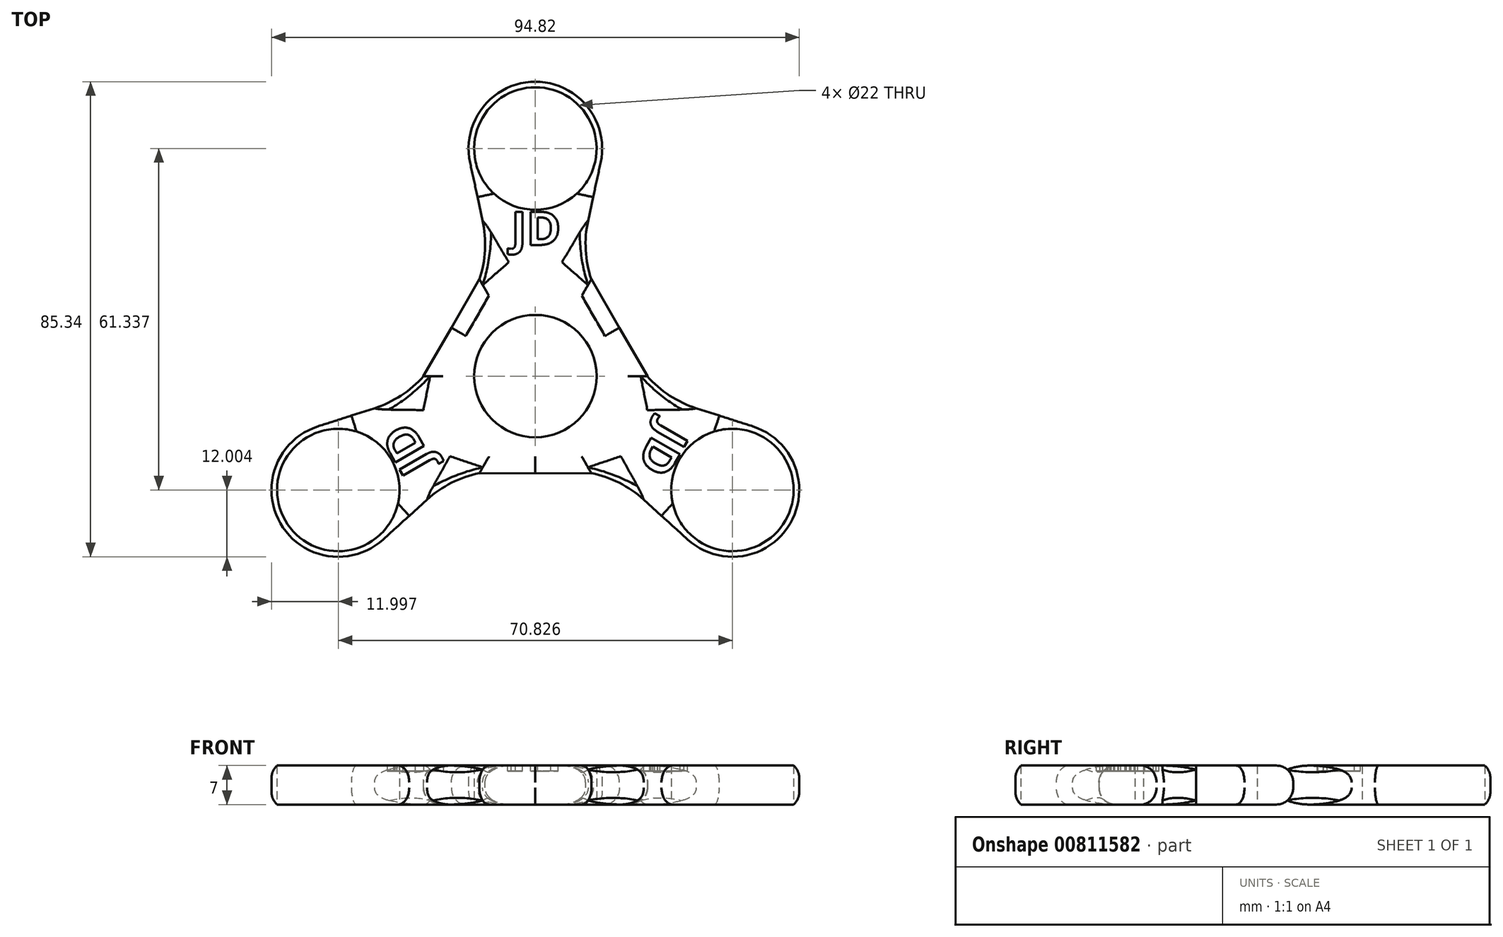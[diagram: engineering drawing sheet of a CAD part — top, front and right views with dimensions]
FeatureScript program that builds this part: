
annotation { "Feature Type Name" : "Feature", "Feature Type Description" : "" }
export const myFeature = defineFeature(function(context is Context, id is Id, definition is map)
    precondition{}
    {
        {
            var Q0;
            Q0=qCreatedBy(makeId("Top.planeOp"),FACE);
            var sketch = newSketch(context, id + "F0", { "sketchPlane" : qUnion([Q0])});
            skCircle(sketch, "E0", {"center": v(0, 0) * mm, "radius": 11 * mm});
            skCircle(sketch, "E1", {"center": v(0, 40.9) * mm, "radius": 11 * mm});
            skLineSegment(sketch, "E2", {"start": v(11, 0) * mm, "end": v(20.17, 0) * mm});
            skLineSegment(sketch, "E3", {"start": v(20.17, 0) * mm, "end": v(7.96, 20.98) * mm});
            skCircle(sketch, "E4", {"center": v(0, 40.9) * mm, "radius": 12 * mm});
            skLineSegment(sketch, "E5", {"start": v(7.96, 20.98) * mm, "end": v(11.73, 38.35) * mm});
            skLineSegment(sketch, "E6.MirrorCS", {"start": v(-11, 0) * mm, "end": v(-20.17, 0) * mm});
            skLineSegment(sketch, "E7.MirrorCS", {"start": v(-20.17, 0) * mm, "end": v(-7.96, 20.98) * mm});
            skLineSegment(sketch, "E8.MirrorCS", {"start": v(-7.96, 20.98) * mm, "end": v(-11.73, 38.35) * mm});
            skSolve(sketch);
        }
        {
            assignVariable(context, id + "F1", {"name" : "Ex", "anyValue" : 7});
        }
        {
            var Q0;
            {var subQ2=sQuery(id+"F0.wireOp",EDGE,"E2");Q0=makeQuery(id+"F0.imprint","IMPRINT",FACE,{"disambiguationData":[TD([[makeQuery(id+"F0.imprint","IMPRINT",EDGE,{"derivedFrom":subQ2}),1.0]])]});}
            var Q1;
            Q1=makeQuery(id+"F0.imprint","IMPRINT",FACE,{"disambiguationData":[TD([[makeQuery(id+"F0.imprint","IMPRINT",EDGE,{"derivedFrom":sQuery(id+"F0.wireOp",EDGE,"E1")}),-1.0]])]});
            extrude(context, id + "F2", {"entities" : qUnion([Q0, Q1]), "depth" : (getVariable(context, 'Ex')) * mm, "offsetDistance" : 25 * mm});
        }
        {
            var Q0;
            Q0=makeQuery(id+"F2.opExtrude","CAP_EDGE",EDGE,{"disambiguationData":[OSD([sQuery(id+"F0.wireOp",EDGE,"E7.MirrorCS")])],"isStart":false});
            var Q1;
            Q1=makeQuery(id+"F2.opExtrude","CAP_EDGE",EDGE,{"disambiguationData":[OSD([sQuery(id+"F0.wireOp",EDGE,"E8.MirrorCS")])],"isStart":false});
            var Q2;
            Q2=makeQuery(id+"F2.opExtrude","CAP_EDGE",EDGE,{"disambiguationData":[OSD([sQuery(id+"F0.wireOp",EDGE,"E3")])],"isStart":false});
            var Q3;
            Q3=makeQuery(id+"F2.opExtrude","CAP_EDGE",EDGE,{"disambiguationData":[OSD([sQuery(id+"F0.wireOp",EDGE,"E8.MirrorCS")])],"isStart":true});
            var Q4;
            Q4=makeQuery(id+"F2.opExtrude","CAP_EDGE",EDGE,{"disambiguationData":[OSD([sQuery(id+"F0.wireOp",EDGE,"E7.MirrorCS")])],"isStart":true});
            var Q5;
            Q5=makeQuery(id+"F2.opExtrude","CAP_EDGE",EDGE,{"disambiguationData":[OSD([sQuery(id+"F0.wireOp",EDGE,"E3")])],"isStart":true});
            fillet(context, id + "F3", {"entities" : qUnion([Q0, Q1, Q2, Q3, Q4, Q5]), "radius" : 3 * mm, "tangentPropagation" : true, "allowEdgeOverflow" : false});
        }
        {
            var Q0;
            Q0=makeQuery(id+"F2.opExtrude","CAP_FACE",FACE,{"disambiguationData":[OSD([sQuery(id+"F0.wireOp",EDGE,"E2"),sQuery(id+"F0.wireOp",EDGE,"E3"),sQuery(id+"F0.wireOp",EDGE,"E5"),sQuery(id+"F0.wireOp",EDGE,"E1"),sQuery(id+"F0.wireOp",EDGE,"E6.MirrorCS"),sQuery(id+"F0.wireOp",EDGE,"E4"),sQuery(id+"F0.wireOp",EDGE,"E0"),sQuery(id+"F0.wireOp",EDGE,"E7.MirrorCS"),sQuery(id+"F0.wireOp",EDGE,"E8.MirrorCS")])],"isStart":false});
            var sketch = newSketch(context, id + "F4", { "sketchPlane" : qUnion([Q0])});
            skText(sketch, "E9", { "text": "JD", "fontName": "NotoSans-Bold.ttf"});
            const initialGuessF4  = {"E9": [-0.00434, 0.02357, 1, 0, 0.006]};
            skSetInitialGuess(sketch, initialGuessF4);
            skSolve(sketch);
        }
        {
            var Q0;
            Q0=makeQuery(id+"F4.imprint","IMPRINT",FACE,{"disambiguationData":[TD([[makeQuery(id+"F4.imprint","IMPRINT",EDGE,{"derivedFrom":sQuery(id+"F4.wireOp",EDGE,"E9.sketch_text.stroke-0")}),-1.0]])]});
            var Q1;
            Q1=makeQuery(id+"F4.imprint","IMPRINT",FACE,{"disambiguationData":[TD([[makeQuery(id+"F4.imprint","IMPRINT",EDGE,{"derivedFrom":sQuery(id+"F4.wireOp",EDGE,"E9.sketch_text.stroke-10")}),-1.0]])]});
            extrude(context, id + "F5", {"entities" : qUnion([Q0, Q1]), "operationType" : NewBodyOperationType.REMOVE, "oppositeDirection" : true, "depth" : 1 * mm, "offsetDistance" : 25 * mm});
        }
        {
            var Q0;
            Q0=makeQuery(id+"F2.opExtrude","SWEPT_BODY",BODY,{"disambiguationData":[OSD([sQuery(id+"F0.wireOp",EDGE,"E2"),sQuery(id+"F0.wireOp",EDGE,"E3"),sQuery(id+"F0.wireOp",EDGE,"E5"),sQuery(id+"F0.wireOp",EDGE,"E1"),sQuery(id+"F0.wireOp",EDGE,"E6.MirrorCS"),sQuery(id+"F0.wireOp",EDGE,"E4"),sQuery(id+"F0.wireOp",EDGE,"E0"),sQuery(id+"F0.wireOp",EDGE,"E7.MirrorCS"),sQuery(id+"F0.wireOp",EDGE,"E8.MirrorCS")])]});
            var Q1;
            Q1=sQuery(id+"F0.wireOp",EDGE,"E0");
            circularPattern(context, id + "F6", {"operationType" : NewBodyOperationType.ADD, "entities" : qUnion([Q0]), "axis" : qUnion([Q1]), "angle" : 360 * degree, "instanceCount" : 3, "equalSpace" : true});
        }
        {
            var Q0;
            Q0=makeQuery(id+"F6.opPattern","COPY",EDGE,{"derivedFrom":makeQuery(id+"F3.opFillet","BLEND_EDGE",EDGE,{"blendedFrom":[makeQuery(id+"F2.opExtrude","CAP_EDGE",EDGE,{"disambiguationData":[OSD([sQuery(id+"F0.wireOp",EDGE,"E3")])],"isStart":false}),makeQuery(id+"F2.opExtrude","CAP_EDGE",EDGE,{"disambiguationData":[OSD([sQuery(id+"F0.wireOp",EDGE,"E5")])],"isStart":false})],"blendedInto":[]}),"instanceName":"1"});
            var Q1;
            Q1=makeQuery(id+"F3.opFillet","BLEND_EDGE",EDGE,{"blendedFrom":[makeQuery(id+"F2.opExtrude","CAP_EDGE",EDGE,{"disambiguationData":[OSD([sQuery(id+"F0.wireOp",EDGE,"E7.MirrorCS")])],"isStart":false}),makeQuery(id+"F2.opExtrude","CAP_EDGE",EDGE,{"disambiguationData":[OSD([sQuery(id+"F0.wireOp",EDGE,"E8.MirrorCS")])],"isStart":false})],"blendedInto":[]});
            var Q2;
            Q2=makeQuery(id+"F6.opPattern","COPY",EDGE,{"derivedFrom":makeQuery(id+"F3.opFillet","BLEND_EDGE",EDGE,{"blendedFrom":[makeQuery(id+"F2.opExtrude","CAP_EDGE",EDGE,{"disambiguationData":[OSD([sQuery(id+"F0.wireOp",EDGE,"E3")])],"isStart":false}),makeQuery(id+"F2.opExtrude","CAP_EDGE",EDGE,{"disambiguationData":[OSD([sQuery(id+"F0.wireOp",EDGE,"E5")])],"isStart":false})],"blendedInto":[]}),"instanceName":"2"});
            var Q3;
            Q3=makeQuery(id+"F6.opPattern","COPY",EDGE,{"derivedFrom":makeQuery(id+"F3.opFillet","BLEND_EDGE",EDGE,{"blendedFrom":[makeQuery(id+"F2.opExtrude","CAP_EDGE",EDGE,{"disambiguationData":[OSD([sQuery(id+"F0.wireOp",EDGE,"E7.MirrorCS")])],"isStart":false}),makeQuery(id+"F2.opExtrude","CAP_EDGE",EDGE,{"disambiguationData":[OSD([sQuery(id+"F0.wireOp",EDGE,"E8.MirrorCS")])],"isStart":false})],"blendedInto":[]}),"instanceName":"1"});
            var Q4;
            Q4=makeQuery(id+"F6.opPattern","COPY",EDGE,{"derivedFrom":makeQuery(id+"F3.opFillet","BLEND_EDGE",EDGE,{"blendedFrom":[makeQuery(id+"F2.opExtrude","CAP_EDGE",EDGE,{"disambiguationData":[OSD([sQuery(id+"F0.wireOp",EDGE,"E7.MirrorCS")])],"isStart":false}),makeQuery(id+"F2.opExtrude","CAP_EDGE",EDGE,{"disambiguationData":[OSD([sQuery(id+"F0.wireOp",EDGE,"E8.MirrorCS")])],"isStart":false})],"blendedInto":[]}),"instanceName":"2"});
            var Q5;
            Q5=makeQuery(id+"F3.opFillet","BLEND_EDGE",EDGE,{"blendedFrom":[makeQuery(id+"F2.opExtrude","CAP_EDGE",EDGE,{"disambiguationData":[OSD([sQuery(id+"F0.wireOp",EDGE,"E3")])],"isStart":false}),makeQuery(id+"F2.opExtrude","CAP_EDGE",EDGE,{"disambiguationData":[OSD([sQuery(id+"F0.wireOp",EDGE,"E5")])],"isStart":false})],"blendedInto":[]});
            fillet(context, id + "F7", {"entities" : qUnion([Q0, Q1, Q2, Q3, Q4, Q5]), "radius" : 20 * mm, "tangentPropagation" : true, "allowEdgeOverflow" : false});
        }
    });
